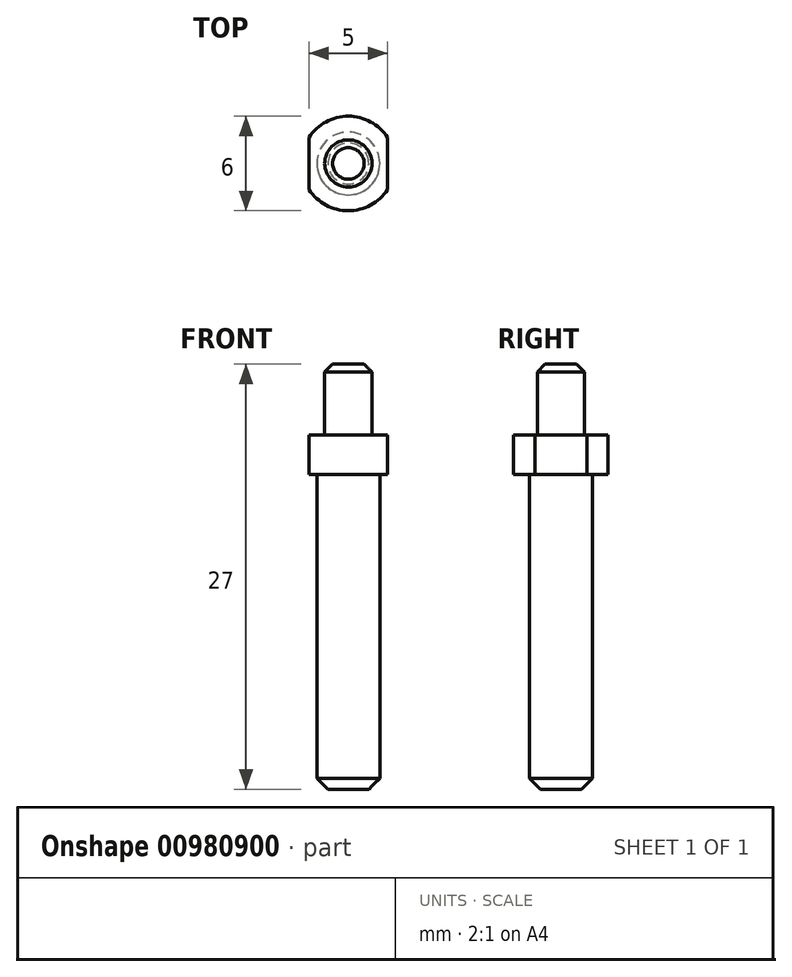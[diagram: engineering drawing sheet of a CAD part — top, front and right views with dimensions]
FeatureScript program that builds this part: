
annotation { "Feature Type Name" : "Feature", "Feature Type Description" : "" }
export const myFeature = defineFeature(function(context is Context, id is Id, definition is map)
    precondition{}
    {
        {
            var Q0;
            Q0=qCreatedBy(makeId("Front.planeOp"),FACE);
            var sketch = newSketch(context, id + "F0", { "sketchPlane" : qUnion([Q0])});
            skLineSegment(sketch, "E0", {"start": v(1.5, 2.5) * mm, "end": v(3, 2.5) * mm});
            skLineSegment(sketch, "E1", {"start": v(3, 2.5) * mm, "end": v(3, 0) * mm});
            skLineSegment(sketch, "E2", {"start": v(3, 0) * mm, "end": v(2, 0) * mm});
            skLineSegment(sketch, "E3", {"start": v(2, 0) * mm, "end": v(2, -20) * mm});
            skLineSegment(sketch, "E4", {"start": v(2, -20) * mm, "end": v(0, -20) * mm});
            skLineSegment(sketch, "E5", {"start": v(0, -20) * mm, "end": v(0, 7) * mm});
            skLineSegment(sketch, "E6", {"start": v(1.5, 2.5) * mm, "end": v(1.5, 7) * mm});
            skLineSegment(sketch, "E7", {"start": v(1.5, 7) * mm, "end": v(0, 7) * mm});
            skSolve(sketch);
        }
        {
            var Q0;
            Q0=makeQuery(id+"F0.imprint","IMPRINT",FACE,{"disambiguationData":[TD([[makeQuery(id+"F0.imprint","IMPRINT",EDGE,{"derivedFrom":sQuery(id+"F0.wireOp",EDGE,"E0")}),-1.0]])]});
            var Q1;
            Q1=sQuery(id+"F0.wireOp",EDGE,"E5");
            revolve(context, id + "F1", {"surfaceOperationType" : NewSurfaceOperationType.NEW, "entities" : qUnion([Q0]), "axis" : qUnion([Q1]), "revolveType" : RevolveType.FULL});
        }
        {
            var Q0;
            Q0=makeQuery(id+"F1.opRevolve","SWEPT_EDGE",EDGE,{"disambiguationData":[OSD([sQuery(id+"F0.wireOp",EDGE,"E6"),sQuery(id+"F0.wireOp",EDGE,"E7")])]});
            chamfer(context, id + "F2", {"entities" : qUnion([Q0]), "width" : 0.5 * mm, "tangentPropagation" : true});
        }
        {
            var Q0;
            Q0=makeQuery(id+"F1.opRevolve","SWEPT_EDGE",EDGE,{"disambiguationData":[OSD([sQuery(id+"F0.wireOp",EDGE,"E3"),sQuery(id+"F0.wireOp",EDGE,"E4")])]});
            chamfer(context, id + "F3", {"entities" : qUnion([Q0]), "width" : 0.7 * mm, "tangentPropagation" : true});
        }
        {
            var Q0;
            Q0=makeQuery(id+"F1.opRevolve","SWEPT_FACE",FACE,{"disambiguationData":[OSD([sQuery(id+"F0.wireOp",EDGE,"E2")])]});
            var sketch = newSketch(context, id + "F4", { "sketchPlane" : qUnion([Q0])});
            skLineSegment(sketch, "E8.bottom", {"start": v(2.5, 3.5) * mm, "end": v(-2.5, 3.5) * mm});
            skLineSegment(sketch, "E8.top", {"start": v(2.5, -3.5) * mm, "end": v(-2.5, -3.5) * mm});
            skLineSegment(sketch, "E8.left", {"start": v(2.5, 3.5) * mm, "end": v(2.5, -3.5) * mm});
            skLineSegment(sketch, "E8.right", {"start": v(-2.5, 3.5) * mm, "end": v(-2.5, -3.5) * mm});
            skPoint(sketch, "E8.middle", {"position": v(0, 0) * mm});
            skSolve(sketch);
        }
        {
            var Q0;
            {var subQ0=sQuery(id+"F4.wireOp",EDGE,"E8.left");var subQ1=makeQuery(id+"F1.opRevolve","SWEPT_EDGE",EDGE,{"disambiguationData":[OSD([sQuery(id+"F0.wireOp",EDGE,"E1"),sQuery(id+"F0.wireOp",EDGE,"E2")])]});var subQ2=makeQuery(id+"F4.imprint","INTERSECT",VERTEX,{"disambiguationData":[OD(0.0)],"derivedFrom":[subQ1,subQ0]});Q0=makeQuery(id+"F4.imprint","IMPRINT",FACE,{"disambiguationData":[TD([[makeQuery(id+"F4.imprint","IMPRINT",EDGE,{"disambiguationData":[TD([[subQ2,-1.0]])],"derivedFrom":subQ0}),1.0]])]});}
            var Q1;
            {var subQ0=sQuery(id+"F4.wireOp",EDGE,"E8.right");var subQ1=makeQuery(id+"F1.opRevolve","SWEPT_EDGE",EDGE,{"disambiguationData":[OSD([sQuery(id+"F0.wireOp",EDGE,"E1"),sQuery(id+"F0.wireOp",EDGE,"E2")])]});var subQ2=makeQuery(id+"F4.imprint","INTERSECT",VERTEX,{"disambiguationData":[OD(0.0)],"derivedFrom":[subQ1,subQ0]});Q1=makeQuery(id+"F4.imprint","IMPRINT",FACE,{"disambiguationData":[TD([[makeQuery(id+"F4.imprint","IMPRINT",EDGE,{"disambiguationData":[TD([[subQ2,-1.0]])],"derivedFrom":subQ0}),-1.0]])]});}
            var Q2;
            Q2=makeQuery(id+"F1.opRevolve","SWEPT_FACE",FACE,{"disambiguationData":[OSD([sQuery(id+"F0.wireOp",EDGE,"E0")])]});
            extrude(context, id + "F5", {"entities" : qUnion([Q0, Q1]), "operationType" : NewBodyOperationType.REMOVE, "endBound" : BoundingType.UP_TO_SURFACE, "oppositeDirection" : true, "depth" : 25 * mm, "endBoundEntityFace" : qUnion([Q2]), "offsetDistance" : 25 * mm});
        }
    });
